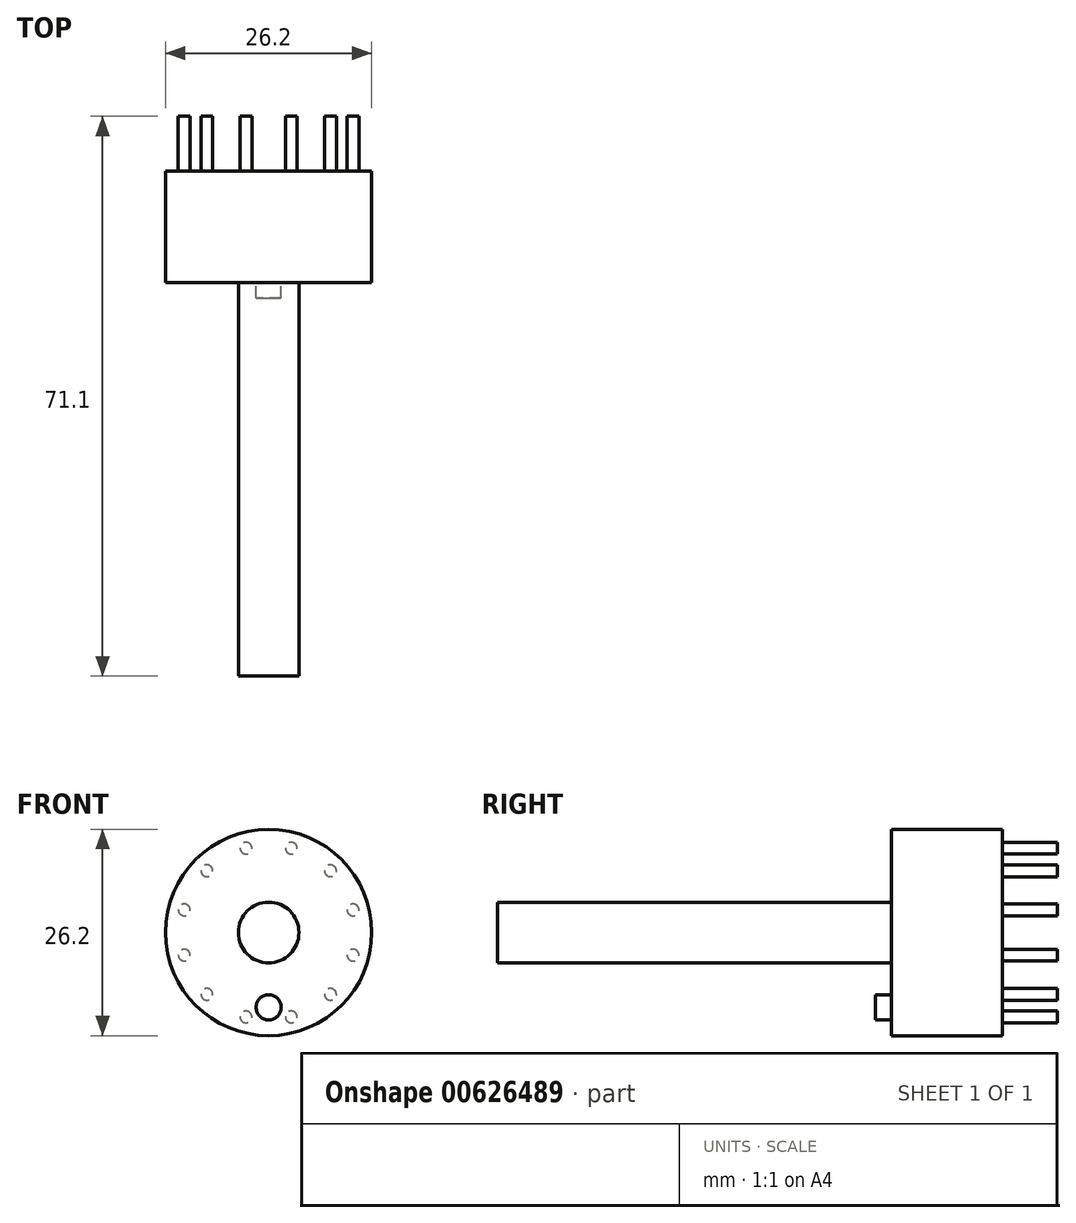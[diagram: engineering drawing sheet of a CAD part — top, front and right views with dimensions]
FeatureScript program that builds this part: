
annotation { "Feature Type Name" : "Feature", "Feature Type Description" : "" }
export const myFeature = defineFeature(function(context is Context, id is Id, definition is map)
    precondition{}
    {
        {
            var Q0;
            Q0=qCreatedBy(makeId("Front.planeOp"),FACE);
            var sketch = newSketch(context, id + "F0", { "sketchPlane" : qUnion([Q0])});
            skCircle(sketch, "E0", {"center": v(0, 0) * mm, "radius": 11.1 * mm, "construction": true});
            skCircle(sketch, "E1", {"center": v(0, 0) * mm, "radius": 3.85 * mm});
            skCircle(sketch, "E2", {"center": v(2.87, 10.72) * mm, "radius": 0.75 * mm});
            skLineSegment(sketch, "E3", {"start": v(2.87, 10.72) * mm, "end": v(3.6, 10.53) * mm, "construction": true});
            skLineSegment(sketch, "E4", {"start": v(2.87, 10.72) * mm, "end": v(3.07, 11.45) * mm, "construction": true});
            skCircle(sketch, "E5.1.0", {"center": v(-2.87, 10.72) * mm, "radius": 0.75 * mm});
            skCircle(sketch, "E5.2.0", {"center": v(-7.85, 7.85) * mm, "radius": 0.75 * mm});
            skCircle(sketch, "E5.3.0", {"center": v(-10.72, 2.87) * mm, "radius": 0.75 * mm});
            skCircle(sketch, "E5.4.0", {"center": v(-10.72, -2.87) * mm, "radius": 0.75 * mm});
            skCircle(sketch, "E5.5.0", {"center": v(-7.85, -7.85) * mm, "radius": 0.75 * mm});
            skCircle(sketch, "E5.6.0", {"center": v(-2.87, -10.72) * mm, "radius": 0.75 * mm});
            skCircle(sketch, "E5.7.0", {"center": v(2.87, -10.72) * mm, "radius": 0.75 * mm});
            skCircle(sketch, "E5.8.0", {"center": v(7.85, -7.85) * mm, "radius": 0.75 * mm});
            skCircle(sketch, "E5.9.0", {"center": v(10.72, -2.87) * mm, "radius": 0.75 * mm});
            skCircle(sketch, "E5.10.0", {"center": v(10.72, 2.87) * mm, "radius": 0.75 * mm});
            skCircle(sketch, "E5.11.0", {"center": v(7.85, 7.85) * mm, "radius": 0.75 * mm});
            skCircle(sketch, "E6", {"center": v(0, -9.5) * mm, "radius": 1.6 * mm});
            skCircle(sketch, "E7", {"center": v(0, 0) * mm, "radius": 13.1 * mm});
            skCircle(sketch, "E8", {"center": v(0, 0) * mm, "radius": 11.1 * mm});
            skSolve(sketch);
        }
        {
            var Q0;
            Q0 = qSketchRegion(id + "F0", true);
            var Q1;
            {var subQ0=sQuery(id+"F0.wireOp",EDGE,"E8");var subQ1=sQuery(id+"F0.wireOp",EDGE,"E2");var subQ2=makeQuery(id+"F0.imprint","INTERSECT",VERTEX,{"disambiguationData":[OD(0.0)],"derivedFrom":[subQ1,subQ0]});Q1=makeQuery(id+"F0.imprint","IMPRINT",FACE,{"disambiguationData":[TD([[makeQuery(id+"F0.imprint","IMPRINT",EDGE,{"disambiguationData":[TD([[subQ2,-1.0]])],"derivedFrom":subQ1}),1.0]])]});}
            var Q2;
            {var subQ0=sQuery(id+"F0.wireOp",EDGE,"E8");var subQ1=sQuery(id+"F0.wireOp",EDGE,"E5.1.0");var subQ2=makeQuery(id+"F0.imprint","INTERSECT",VERTEX,{"disambiguationData":[OD(0.0)],"derivedFrom":[subQ1,subQ0]});Q2=makeQuery(id+"F0.imprint","IMPRINT",FACE,{"disambiguationData":[TD([[makeQuery(id+"F0.imprint","IMPRINT",EDGE,{"disambiguationData":[TD([[subQ2,-1.0]])],"derivedFrom":subQ1}),1.0]])]});}
            var Q3;
            {var subQ0=sQuery(id+"F0.wireOp",EDGE,"E8");var subQ1=sQuery(id+"F0.wireOp",EDGE,"E5.11.0");var subQ2=makeQuery(id+"F0.imprint","INTERSECT",VERTEX,{"disambiguationData":[OD(0.0)],"derivedFrom":[subQ1,subQ0]});Q3=makeQuery(id+"F0.imprint","IMPRINT",FACE,{"disambiguationData":[TD([[makeQuery(id+"F0.imprint","IMPRINT",EDGE,{"disambiguationData":[TD([[subQ2,-1.0]])],"derivedFrom":subQ1}),1.0]])]});}
            var Q4;
            {var subQ0=sQuery(id+"F0.wireOp",EDGE,"E8");var subQ1=sQuery(id+"F0.wireOp",EDGE,"E5.10.0");var subQ2=makeQuery(id+"F0.imprint","INTERSECT",VERTEX,{"disambiguationData":[OD(0.0)],"derivedFrom":[subQ1,subQ0]});Q4=makeQuery(id+"F0.imprint","IMPRINT",FACE,{"disambiguationData":[TD([[makeQuery(id+"F0.imprint","IMPRINT",EDGE,{"disambiguationData":[TD([[subQ2,1.0]])],"derivedFrom":subQ1}),1.0]])]});}
            var Q5;
            {var subQ0=sQuery(id+"F0.wireOp",EDGE,"E8");var subQ1=sQuery(id+"F0.wireOp",EDGE,"E5.9.0");var subQ2=makeQuery(id+"F0.imprint","INTERSECT",VERTEX,{"disambiguationData":[OD(0.0)],"derivedFrom":[subQ1,subQ0]});Q5=makeQuery(id+"F0.imprint","IMPRINT",FACE,{"disambiguationData":[TD([[makeQuery(id+"F0.imprint","IMPRINT",EDGE,{"disambiguationData":[TD([[subQ2,-1.0]])],"derivedFrom":subQ1}),1.0]])]});}
            var Q6;
            {var subQ0=sQuery(id+"F0.wireOp",EDGE,"E8");var subQ1=sQuery(id+"F0.wireOp",EDGE,"E5.8.0");var subQ2=makeQuery(id+"F0.imprint","INTERSECT",VERTEX,{"disambiguationData":[OD(0.0)],"derivedFrom":[subQ1,subQ0]});Q6=makeQuery(id+"F0.imprint","IMPRINT",FACE,{"disambiguationData":[TD([[makeQuery(id+"F0.imprint","IMPRINT",EDGE,{"disambiguationData":[TD([[subQ2,-1.0]])],"derivedFrom":subQ1}),1.0]])]});}
            var Q7;
            {var subQ0=sQuery(id+"F0.wireOp",EDGE,"E8");var subQ1=sQuery(id+"F0.wireOp",EDGE,"E5.7.0");var subQ2=makeQuery(id+"F0.imprint","INTERSECT",VERTEX,{"disambiguationData":[OD(0.0)],"derivedFrom":[subQ1,subQ0]});Q7=makeQuery(id+"F0.imprint","IMPRINT",FACE,{"disambiguationData":[TD([[makeQuery(id+"F0.imprint","IMPRINT",EDGE,{"disambiguationData":[TD([[subQ2,-1.0]])],"derivedFrom":subQ1}),1.0]])]});}
            var Q8;
            {var subQ0=sQuery(id+"F0.wireOp",EDGE,"E8");var subQ1=sQuery(id+"F0.wireOp",EDGE,"E5.2.0");var subQ2=makeQuery(id+"F0.imprint","INTERSECT",VERTEX,{"disambiguationData":[OD(0.0)],"derivedFrom":[subQ1,subQ0]});Q8=makeQuery(id+"F0.imprint","IMPRINT",FACE,{"disambiguationData":[TD([[makeQuery(id+"F0.imprint","IMPRINT",EDGE,{"disambiguationData":[TD([[subQ2,-1.0]])],"derivedFrom":subQ1}),1.0]])]});}
            var Q9;
            {var subQ0=sQuery(id+"F0.wireOp",EDGE,"E8");var subQ1=sQuery(id+"F0.wireOp",EDGE,"E5.3.0");var subQ2=makeQuery(id+"F0.imprint","INTERSECT",VERTEX,{"disambiguationData":[OD(0.0)],"derivedFrom":[subQ1,subQ0]});Q9=makeQuery(id+"F0.imprint","IMPRINT",FACE,{"disambiguationData":[TD([[makeQuery(id+"F0.imprint","IMPRINT",EDGE,{"disambiguationData":[TD([[subQ2,-1.0]])],"derivedFrom":subQ1}),1.0]])]});}
            var Q10;
            {var subQ0=sQuery(id+"F0.wireOp",EDGE,"E8");var subQ1=sQuery(id+"F0.wireOp",EDGE,"E5.4.0");var subQ2=makeQuery(id+"F0.imprint","INTERSECT",VERTEX,{"disambiguationData":[OD(0.0)],"derivedFrom":[subQ1,subQ0]});Q10=makeQuery(id+"F0.imprint","IMPRINT",FACE,{"disambiguationData":[TD([[makeQuery(id+"F0.imprint","IMPRINT",EDGE,{"disambiguationData":[TD([[subQ2,-1.0]])],"derivedFrom":subQ1}),1.0]])]});}
            var Q11;
            {var subQ0=sQuery(id+"F0.wireOp",EDGE,"E8");var subQ1=sQuery(id+"F0.wireOp",EDGE,"E5.5.0");var subQ2=makeQuery(id+"F0.imprint","INTERSECT",VERTEX,{"disambiguationData":[OD(0.0)],"derivedFrom":[subQ1,subQ0]});Q11=makeQuery(id+"F0.imprint","IMPRINT",FACE,{"disambiguationData":[TD([[makeQuery(id+"F0.imprint","IMPRINT",EDGE,{"disambiguationData":[TD([[subQ2,-1.0]])],"derivedFrom":subQ1}),1.0]])]});}
            var Q12;
            {var subQ0=sQuery(id+"F0.wireOp",EDGE,"E8");var subQ1=sQuery(id+"F0.wireOp",EDGE,"E5.6.0");var subQ2=makeQuery(id+"F0.imprint","INTERSECT",VERTEX,{"disambiguationData":[OD(0.0)],"derivedFrom":[subQ1,subQ0]});Q12=makeQuery(id+"F0.imprint","IMPRINT",FACE,{"disambiguationData":[TD([[makeQuery(id+"F0.imprint","IMPRINT",EDGE,{"disambiguationData":[TD([[subQ2,-1.0]])],"derivedFrom":subQ1}),1.0]])]});}
            var Q13;
            Q13=makeQuery(id+"F0.imprint","IMPRINT",FACE,{"disambiguationData":[TD([[makeQuery(id+"F0.imprint","IMPRINT",EDGE,{"derivedFrom":sQuery(id+"F0.wireOp",EDGE,"E1")}),-1.0]])]});
            var Q14;
            {var subQ0=sQuery(id+"F0.wireOp",EDGE,"E8");var subQ1=sQuery(id+"F0.wireOp",EDGE,"E5.2.0");var subQ2=makeQuery(id+"F0.imprint","INTERSECT",VERTEX,{"disambiguationData":[OD(0.0)],"derivedFrom":[subQ1,subQ0]});Q14=makeQuery(id+"F0.imprint","IMPRINT",FACE,{"disambiguationData":[TD([[makeQuery(id+"F0.imprint","IMPRINT",EDGE,{"disambiguationData":[TD([[subQ2,1.0]])],"derivedFrom":subQ1}),1.0]])]});}
            var Q15;
            {var subQ0=sQuery(id+"F0.wireOp",EDGE,"E8");var subQ1=sQuery(id+"F0.wireOp",EDGE,"E5.1.0");var subQ2=makeQuery(id+"F0.imprint","INTERSECT",VERTEX,{"disambiguationData":[OD(0.0)],"derivedFrom":[subQ1,subQ0]});Q15=makeQuery(id+"F0.imprint","IMPRINT",FACE,{"disambiguationData":[TD([[makeQuery(id+"F0.imprint","IMPRINT",EDGE,{"disambiguationData":[TD([[subQ2,1.0]])],"derivedFrom":subQ1}),1.0]])]});}
            var Q16;
            {var subQ0=sQuery(id+"F0.wireOp",EDGE,"E8");var subQ1=sQuery(id+"F0.wireOp",EDGE,"E2");var subQ2=makeQuery(id+"F0.imprint","INTERSECT",VERTEX,{"disambiguationData":[OD(0.0)],"derivedFrom":[subQ1,subQ0]});Q16=makeQuery(id+"F0.imprint","IMPRINT",FACE,{"disambiguationData":[TD([[makeQuery(id+"F0.imprint","IMPRINT",EDGE,{"disambiguationData":[TD([[subQ2,1.0]])],"derivedFrom":subQ1}),1.0]])]});}
            var Q17;
            {var subQ0=sQuery(id+"F0.wireOp",EDGE,"E8");var subQ1=sQuery(id+"F0.wireOp",EDGE,"E5.11.0");var subQ2=makeQuery(id+"F0.imprint","INTERSECT",VERTEX,{"disambiguationData":[OD(0.0)],"derivedFrom":[subQ1,subQ0]});Q17=makeQuery(id+"F0.imprint","IMPRINT",FACE,{"disambiguationData":[TD([[makeQuery(id+"F0.imprint","IMPRINT",EDGE,{"disambiguationData":[TD([[subQ2,1.0]])],"derivedFrom":subQ1}),1.0]])]});}
            var Q18;
            {var subQ0=sQuery(id+"F0.wireOp",EDGE,"E8");var subQ1=sQuery(id+"F0.wireOp",EDGE,"E5.10.0");var subQ2=makeQuery(id+"F0.imprint","INTERSECT",VERTEX,{"disambiguationData":[OD(0.0)],"derivedFrom":[subQ1,subQ0]});Q18=makeQuery(id+"F0.imprint","IMPRINT",FACE,{"disambiguationData":[TD([[makeQuery(id+"F0.imprint","IMPRINT",EDGE,{"disambiguationData":[TD([[subQ2,-1.0]])],"derivedFrom":subQ1}),1.0]])]});}
            var Q19;
            {var subQ0=sQuery(id+"F0.wireOp",EDGE,"E8");var subQ1=sQuery(id+"F0.wireOp",EDGE,"E5.9.0");var subQ2=makeQuery(id+"F0.imprint","INTERSECT",VERTEX,{"disambiguationData":[OD(0.0)],"derivedFrom":[subQ1,subQ0]});Q19=makeQuery(id+"F0.imprint","IMPRINT",FACE,{"disambiguationData":[TD([[makeQuery(id+"F0.imprint","IMPRINT",EDGE,{"disambiguationData":[TD([[subQ2,1.0]])],"derivedFrom":subQ1}),1.0]])]});}
            var Q20;
            {var subQ0=sQuery(id+"F0.wireOp",EDGE,"E8");var subQ1=sQuery(id+"F0.wireOp",EDGE,"E5.8.0");var subQ2=makeQuery(id+"F0.imprint","INTERSECT",VERTEX,{"disambiguationData":[OD(0.0)],"derivedFrom":[subQ1,subQ0]});Q20=makeQuery(id+"F0.imprint","IMPRINT",FACE,{"disambiguationData":[TD([[makeQuery(id+"F0.imprint","IMPRINT",EDGE,{"disambiguationData":[TD([[subQ2,1.0]])],"derivedFrom":subQ1}),1.0]])]});}
            var Q21;
            {var subQ0=sQuery(id+"F0.wireOp",EDGE,"E8");var subQ1=sQuery(id+"F0.wireOp",EDGE,"E5.7.0");var subQ2=makeQuery(id+"F0.imprint","INTERSECT",VERTEX,{"disambiguationData":[OD(0.0)],"derivedFrom":[subQ1,subQ0]});Q21=makeQuery(id+"F0.imprint","IMPRINT",FACE,{"disambiguationData":[TD([[makeQuery(id+"F0.imprint","IMPRINT",EDGE,{"disambiguationData":[TD([[subQ2,1.0]])],"derivedFrom":subQ1}),1.0]])]});}
            var Q22;
            {var subQ0=sQuery(id+"F0.wireOp",EDGE,"E8");var subQ1=sQuery(id+"F0.wireOp",EDGE,"E5.6.0");var subQ2=makeQuery(id+"F0.imprint","INTERSECT",VERTEX,{"disambiguationData":[OD(0.0)],"derivedFrom":[subQ1,subQ0]});Q22=makeQuery(id+"F0.imprint","IMPRINT",FACE,{"disambiguationData":[TD([[makeQuery(id+"F0.imprint","IMPRINT",EDGE,{"disambiguationData":[TD([[subQ2,1.0]])],"derivedFrom":subQ1}),1.0]])]});}
            var Q23;
            {var subQ0=sQuery(id+"F0.wireOp",EDGE,"E8");var subQ1=sQuery(id+"F0.wireOp",EDGE,"E5.5.0");var subQ2=makeQuery(id+"F0.imprint","INTERSECT",VERTEX,{"disambiguationData":[OD(0.0)],"derivedFrom":[subQ1,subQ0]});Q23=makeQuery(id+"F0.imprint","IMPRINT",FACE,{"disambiguationData":[TD([[makeQuery(id+"F0.imprint","IMPRINT",EDGE,{"disambiguationData":[TD([[subQ2,1.0]])],"derivedFrom":subQ1}),1.0]])]});}
            var Q24;
            {var subQ0=sQuery(id+"F0.wireOp",EDGE,"E8");var subQ1=sQuery(id+"F0.wireOp",EDGE,"E5.4.0");var subQ2=makeQuery(id+"F0.imprint","INTERSECT",VERTEX,{"disambiguationData":[OD(0.0)],"derivedFrom":[subQ1,subQ0]});Q24=makeQuery(id+"F0.imprint","IMPRINT",FACE,{"disambiguationData":[TD([[makeQuery(id+"F0.imprint","IMPRINT",EDGE,{"disambiguationData":[TD([[subQ2,1.0]])],"derivedFrom":subQ1}),1.0]])]});}
            var Q25;
            {var subQ0=sQuery(id+"F0.wireOp",EDGE,"E8");var subQ1=sQuery(id+"F0.wireOp",EDGE,"E5.3.0");var subQ2=makeQuery(id+"F0.imprint","INTERSECT",VERTEX,{"disambiguationData":[OD(0.0)],"derivedFrom":[subQ1,subQ0]});Q25=makeQuery(id+"F0.imprint","IMPRINT",FACE,{"disambiguationData":[TD([[makeQuery(id+"F0.imprint","IMPRINT",EDGE,{"disambiguationData":[TD([[subQ2,1.0]])],"derivedFrom":subQ1}),1.0]])]});}
            extrude(context, id + "F1", {"entities" : qUnion([Q0, Q1, Q2, Q3, Q4, Q5, Q6, Q7, Q8, Q9, Q10, Q11, Q12, Q13, Q14, Q15, Q16, Q17, Q18, Q19, Q20, Q21, Q22, Q23, Q24, Q25]), "depth" : 14.1 * mm, "offsetDistance" : 25 * mm});
        }
        {
            var Q0;
            Q0=makeQuery(id+"F0.imprint","IMPRINT",FACE,{"disambiguationData":[TD([[makeQuery(id+"F0.imprint","IMPRINT",EDGE,{"derivedFrom":sQuery(id+"F0.wireOp",EDGE,"E6")}),1.0]])]});
            var Q1;
            Q1=makeQuery(id+"F1.opExtrude","CAP_FACE",FACE,{"disambiguationData":[OSD([sQuery(id+"F0.wireOp",EDGE,"E1"),sQuery(id+"F0.wireOp",EDGE,"E6"),sQuery(id+"F0.wireOp",EDGE,"E7")])],"isStart":false});
            extrude(context, id + "F2", {"entities" : qUnion([Q0]), "operationType" : NewBodyOperationType.ADD, "endBound" : BoundingType.UP_TO_SURFACE, "depth" : 25 * mm, "endBoundEntityFace" : qUnion([Q1]), "hasOffset" : true, "offsetDistance" : -2 * mm});
        }
        {
            var Q0;
            Q0=makeQuery(id+"F0.imprint","IMPRINT",FACE,{"disambiguationData":[TD([[makeQuery(id+"F0.imprint","IMPRINT",EDGE,{"derivedFrom":sQuery(id+"F0.wireOp",EDGE,"E1")}),1.0]])]});
            var Q1;
            Q1=makeQuery(id+"F1.opExtrude","CAP_FACE",FACE,{"disambiguationData":[OSD([sQuery(id+"F0.wireOp",EDGE,"E1"),sQuery(id+"F0.wireOp",EDGE,"E6"),sQuery(id+"F0.wireOp",EDGE,"E7")])],"isStart":false});
            extrude(context, id + "F3", {"entities" : qUnion([Q0]), "operationType" : NewBodyOperationType.ADD, "endBound" : BoundingType.UP_TO_SURFACE, "depth" : 34.9 * mm, "endBoundEntityFace" : qUnion([Q1]), "hasOffset" : true, "offsetDistance" : -50 * mm});
        }
        {
            var Q0;
            {var subQ0=sQuery(id+"F0.wireOp",EDGE,"E8");var subQ1=sQuery(id+"F0.wireOp",EDGE,"E5.7.0");var subQ2=makeQuery(id+"F0.imprint","INTERSECT",VERTEX,{"disambiguationData":[OD(0.0)],"derivedFrom":[subQ1,subQ0]});Q0=makeQuery(id+"F0.imprint","IMPRINT",FACE,{"disambiguationData":[TD([[makeQuery(id+"F0.imprint","IMPRINT",EDGE,{"disambiguationData":[TD([[subQ2,1.0]])],"derivedFrom":subQ1}),1.0]])]});}
            var Q1;
            {var subQ0=sQuery(id+"F0.wireOp",EDGE,"E8");var subQ1=sQuery(id+"F0.wireOp",EDGE,"E5.7.0");var subQ2=makeQuery(id+"F0.imprint","INTERSECT",VERTEX,{"disambiguationData":[OD(0.0)],"derivedFrom":[subQ1,subQ0]});Q1=makeQuery(id+"F0.imprint","IMPRINT",FACE,{"disambiguationData":[TD([[makeQuery(id+"F0.imprint","IMPRINT",EDGE,{"disambiguationData":[TD([[subQ2,-1.0]])],"derivedFrom":subQ1}),1.0]])]});}
            var Q2;
            {var subQ0=sQuery(id+"F0.wireOp",EDGE,"E8");var subQ1=sQuery(id+"F0.wireOp",EDGE,"E5.8.0");var subQ2=makeQuery(id+"F0.imprint","INTERSECT",VERTEX,{"disambiguationData":[OD(0.0)],"derivedFrom":[subQ1,subQ0]});Q2=makeQuery(id+"F0.imprint","IMPRINT",FACE,{"disambiguationData":[TD([[makeQuery(id+"F0.imprint","IMPRINT",EDGE,{"disambiguationData":[TD([[subQ2,1.0]])],"derivedFrom":subQ1}),1.0]])]});}
            var Q3;
            {var subQ0=sQuery(id+"F0.wireOp",EDGE,"E8");var subQ1=sQuery(id+"F0.wireOp",EDGE,"E5.8.0");var subQ2=makeQuery(id+"F0.imprint","INTERSECT",VERTEX,{"disambiguationData":[OD(0.0)],"derivedFrom":[subQ1,subQ0]});Q3=makeQuery(id+"F0.imprint","IMPRINT",FACE,{"disambiguationData":[TD([[makeQuery(id+"F0.imprint","IMPRINT",EDGE,{"disambiguationData":[TD([[subQ2,-1.0]])],"derivedFrom":subQ1}),1.0]])]});}
            var Q4;
            {var subQ0=sQuery(id+"F0.wireOp",EDGE,"E8");var subQ1=sQuery(id+"F0.wireOp",EDGE,"E5.9.0");var subQ2=makeQuery(id+"F0.imprint","INTERSECT",VERTEX,{"disambiguationData":[OD(0.0)],"derivedFrom":[subQ1,subQ0]});Q4=makeQuery(id+"F0.imprint","IMPRINT",FACE,{"disambiguationData":[TD([[makeQuery(id+"F0.imprint","IMPRINT",EDGE,{"disambiguationData":[TD([[subQ2,1.0]])],"derivedFrom":subQ1}),1.0]])]});}
            var Q5;
            {var subQ0=sQuery(id+"F0.wireOp",EDGE,"E8");var subQ1=sQuery(id+"F0.wireOp",EDGE,"E5.9.0");var subQ2=makeQuery(id+"F0.imprint","INTERSECT",VERTEX,{"disambiguationData":[OD(0.0)],"derivedFrom":[subQ1,subQ0]});Q5=makeQuery(id+"F0.imprint","IMPRINT",FACE,{"disambiguationData":[TD([[makeQuery(id+"F0.imprint","IMPRINT",EDGE,{"disambiguationData":[TD([[subQ2,-1.0]])],"derivedFrom":subQ1}),1.0]])]});}
            var Q6;
            {var subQ0=sQuery(id+"F0.wireOp",EDGE,"E8");var subQ1=sQuery(id+"F0.wireOp",EDGE,"E5.6.0");var subQ2=makeQuery(id+"F0.imprint","INTERSECT",VERTEX,{"disambiguationData":[OD(0.0)],"derivedFrom":[subQ1,subQ0]});Q6=makeQuery(id+"F0.imprint","IMPRINT",FACE,{"disambiguationData":[TD([[makeQuery(id+"F0.imprint","IMPRINT",EDGE,{"disambiguationData":[TD([[subQ2,-1.0]])],"derivedFrom":subQ1}),1.0]])]});}
            var Q7;
            {var subQ0=sQuery(id+"F0.wireOp",EDGE,"E8");var subQ1=sQuery(id+"F0.wireOp",EDGE,"E5.6.0");var subQ2=makeQuery(id+"F0.imprint","INTERSECT",VERTEX,{"disambiguationData":[OD(0.0)],"derivedFrom":[subQ1,subQ0]});Q7=makeQuery(id+"F0.imprint","IMPRINT",FACE,{"disambiguationData":[TD([[makeQuery(id+"F0.imprint","IMPRINT",EDGE,{"disambiguationData":[TD([[subQ2,1.0]])],"derivedFrom":subQ1}),1.0]])]});}
            var Q8;
            {var subQ0=sQuery(id+"F0.wireOp",EDGE,"E8");var subQ1=sQuery(id+"F0.wireOp",EDGE,"E5.5.0");var subQ2=makeQuery(id+"F0.imprint","INTERSECT",VERTEX,{"disambiguationData":[OD(0.0)],"derivedFrom":[subQ1,subQ0]});Q8=makeQuery(id+"F0.imprint","IMPRINT",FACE,{"disambiguationData":[TD([[makeQuery(id+"F0.imprint","IMPRINT",EDGE,{"disambiguationData":[TD([[subQ2,-1.0]])],"derivedFrom":subQ1}),1.0]])]});}
            var Q9;
            {var subQ0=sQuery(id+"F0.wireOp",EDGE,"E8");var subQ1=sQuery(id+"F0.wireOp",EDGE,"E5.5.0");var subQ2=makeQuery(id+"F0.imprint","INTERSECT",VERTEX,{"disambiguationData":[OD(0.0)],"derivedFrom":[subQ1,subQ0]});Q9=makeQuery(id+"F0.imprint","IMPRINT",FACE,{"disambiguationData":[TD([[makeQuery(id+"F0.imprint","IMPRINT",EDGE,{"disambiguationData":[TD([[subQ2,1.0]])],"derivedFrom":subQ1}),1.0]])]});}
            var Q10;
            {var subQ0=sQuery(id+"F0.wireOp",EDGE,"E8");var subQ1=sQuery(id+"F0.wireOp",EDGE,"E5.4.0");var subQ2=makeQuery(id+"F0.imprint","INTERSECT",VERTEX,{"disambiguationData":[OD(0.0)],"derivedFrom":[subQ1,subQ0]});Q10=makeQuery(id+"F0.imprint","IMPRINT",FACE,{"disambiguationData":[TD([[makeQuery(id+"F0.imprint","IMPRINT",EDGE,{"disambiguationData":[TD([[subQ2,1.0]])],"derivedFrom":subQ1}),1.0]])]});}
            var Q11;
            {var subQ0=sQuery(id+"F0.wireOp",EDGE,"E8");var subQ1=sQuery(id+"F0.wireOp",EDGE,"E5.4.0");var subQ2=makeQuery(id+"F0.imprint","INTERSECT",VERTEX,{"disambiguationData":[OD(0.0)],"derivedFrom":[subQ1,subQ0]});Q11=makeQuery(id+"F0.imprint","IMPRINT",FACE,{"disambiguationData":[TD([[makeQuery(id+"F0.imprint","IMPRINT",EDGE,{"disambiguationData":[TD([[subQ2,-1.0]])],"derivedFrom":subQ1}),1.0]])]});}
            var Q12;
            {var subQ0=sQuery(id+"F0.wireOp",EDGE,"E8");var subQ1=sQuery(id+"F0.wireOp",EDGE,"E5.3.0");var subQ2=makeQuery(id+"F0.imprint","INTERSECT",VERTEX,{"disambiguationData":[OD(0.0)],"derivedFrom":[subQ1,subQ0]});Q12=makeQuery(id+"F0.imprint","IMPRINT",FACE,{"disambiguationData":[TD([[makeQuery(id+"F0.imprint","IMPRINT",EDGE,{"disambiguationData":[TD([[subQ2,1.0]])],"derivedFrom":subQ1}),1.0]])]});}
            var Q13;
            {var subQ0=sQuery(id+"F0.wireOp",EDGE,"E8");var subQ1=sQuery(id+"F0.wireOp",EDGE,"E5.3.0");var subQ2=makeQuery(id+"F0.imprint","INTERSECT",VERTEX,{"disambiguationData":[OD(0.0)],"derivedFrom":[subQ1,subQ0]});Q13=makeQuery(id+"F0.imprint","IMPRINT",FACE,{"disambiguationData":[TD([[makeQuery(id+"F0.imprint","IMPRINT",EDGE,{"disambiguationData":[TD([[subQ2,-1.0]])],"derivedFrom":subQ1}),1.0]])]});}
            var Q14;
            {var subQ0=sQuery(id+"F0.wireOp",EDGE,"E8");var subQ1=sQuery(id+"F0.wireOp",EDGE,"E5.2.0");var subQ2=makeQuery(id+"F0.imprint","INTERSECT",VERTEX,{"disambiguationData":[OD(0.0)],"derivedFrom":[subQ1,subQ0]});Q14=makeQuery(id+"F0.imprint","IMPRINT",FACE,{"disambiguationData":[TD([[makeQuery(id+"F0.imprint","IMPRINT",EDGE,{"disambiguationData":[TD([[subQ2,1.0]])],"derivedFrom":subQ1}),1.0]])]});}
            var Q15;
            {var subQ0=sQuery(id+"F0.wireOp",EDGE,"E8");var subQ1=sQuery(id+"F0.wireOp",EDGE,"E5.2.0");var subQ2=makeQuery(id+"F0.imprint","INTERSECT",VERTEX,{"disambiguationData":[OD(0.0)],"derivedFrom":[subQ1,subQ0]});Q15=makeQuery(id+"F0.imprint","IMPRINT",FACE,{"disambiguationData":[TD([[makeQuery(id+"F0.imprint","IMPRINT",EDGE,{"disambiguationData":[TD([[subQ2,-1.0]])],"derivedFrom":subQ1}),1.0]])]});}
            var Q16;
            {var subQ0=sQuery(id+"F0.wireOp",EDGE,"E8");var subQ1=sQuery(id+"F0.wireOp",EDGE,"E2");var subQ2=makeQuery(id+"F0.imprint","INTERSECT",VERTEX,{"disambiguationData":[OD(0.0)],"derivedFrom":[subQ1,subQ0]});Q16=makeQuery(id+"F0.imprint","IMPRINT",FACE,{"disambiguationData":[TD([[makeQuery(id+"F0.imprint","IMPRINT",EDGE,{"disambiguationData":[TD([[subQ2,1.0]])],"derivedFrom":subQ1}),1.0]])]});}
            var Q17;
            {var subQ0=sQuery(id+"F0.wireOp",EDGE,"E8");var subQ1=sQuery(id+"F0.wireOp",EDGE,"E2");var subQ2=makeQuery(id+"F0.imprint","INTERSECT",VERTEX,{"disambiguationData":[OD(0.0)],"derivedFrom":[subQ1,subQ0]});Q17=makeQuery(id+"F0.imprint","IMPRINT",FACE,{"disambiguationData":[TD([[makeQuery(id+"F0.imprint","IMPRINT",EDGE,{"disambiguationData":[TD([[subQ2,-1.0]])],"derivedFrom":subQ1}),1.0]])]});}
            var Q18;
            {var subQ0=sQuery(id+"F0.wireOp",EDGE,"E8");var subQ1=sQuery(id+"F0.wireOp",EDGE,"E5.10.0");var subQ2=makeQuery(id+"F0.imprint","INTERSECT",VERTEX,{"disambiguationData":[OD(0.0)],"derivedFrom":[subQ1,subQ0]});Q18=makeQuery(id+"F0.imprint","IMPRINT",FACE,{"disambiguationData":[TD([[makeQuery(id+"F0.imprint","IMPRINT",EDGE,{"disambiguationData":[TD([[subQ2,-1.0]])],"derivedFrom":subQ1}),1.0]])]});}
            var Q19;
            {var subQ0=sQuery(id+"F0.wireOp",EDGE,"E8");var subQ1=sQuery(id+"F0.wireOp",EDGE,"E5.10.0");var subQ2=makeQuery(id+"F0.imprint","INTERSECT",VERTEX,{"disambiguationData":[OD(0.0)],"derivedFrom":[subQ1,subQ0]});Q19=makeQuery(id+"F0.imprint","IMPRINT",FACE,{"disambiguationData":[TD([[makeQuery(id+"F0.imprint","IMPRINT",EDGE,{"disambiguationData":[TD([[subQ2,1.0]])],"derivedFrom":subQ1}),1.0]])]});}
            var Q20;
            {var subQ0=sQuery(id+"F0.wireOp",EDGE,"E8");var subQ1=sQuery(id+"F0.wireOp",EDGE,"E5.11.0");var subQ2=makeQuery(id+"F0.imprint","INTERSECT",VERTEX,{"disambiguationData":[OD(0.0)],"derivedFrom":[subQ1,subQ0]});Q20=makeQuery(id+"F0.imprint","IMPRINT",FACE,{"disambiguationData":[TD([[makeQuery(id+"F0.imprint","IMPRINT",EDGE,{"disambiguationData":[TD([[subQ2,1.0]])],"derivedFrom":subQ1}),1.0]])]});}
            var Q21;
            {var subQ0=sQuery(id+"F0.wireOp",EDGE,"E8");var subQ1=sQuery(id+"F0.wireOp",EDGE,"E5.11.0");var subQ2=makeQuery(id+"F0.imprint","INTERSECT",VERTEX,{"disambiguationData":[OD(0.0)],"derivedFrom":[subQ1,subQ0]});Q21=makeQuery(id+"F0.imprint","IMPRINT",FACE,{"disambiguationData":[TD([[makeQuery(id+"F0.imprint","IMPRINT",EDGE,{"disambiguationData":[TD([[subQ2,-1.0]])],"derivedFrom":subQ1}),1.0]])]});}
            var Q22;
            {var subQ0=sQuery(id+"F0.wireOp",EDGE,"E8");var subQ1=sQuery(id+"F0.wireOp",EDGE,"E5.1.0");var subQ2=makeQuery(id+"F0.imprint","INTERSECT",VERTEX,{"disambiguationData":[OD(0.0)],"derivedFrom":[subQ1,subQ0]});Q22=makeQuery(id+"F0.imprint","IMPRINT",FACE,{"disambiguationData":[TD([[makeQuery(id+"F0.imprint","IMPRINT",EDGE,{"disambiguationData":[TD([[subQ2,1.0]])],"derivedFrom":subQ1}),1.0]])]});}
            var Q23;
            {var subQ0=sQuery(id+"F0.wireOp",EDGE,"E8");var subQ1=sQuery(id+"F0.wireOp",EDGE,"E5.1.0");var subQ2=makeQuery(id+"F0.imprint","INTERSECT",VERTEX,{"disambiguationData":[OD(0.0)],"derivedFrom":[subQ1,subQ0]});Q23=makeQuery(id+"F0.imprint","IMPRINT",FACE,{"disambiguationData":[TD([[makeQuery(id+"F0.imprint","IMPRINT",EDGE,{"disambiguationData":[TD([[subQ2,-1.0]])],"derivedFrom":subQ1}),1.0]])]});}
            extrude(context, id + "F4", {"entities" : qUnion([Q0, Q1, Q2, Q3, Q4, Q5, Q6, Q7, Q8, Q9, Q10, Q11, Q12, Q13, Q14, Q15, Q16, Q17, Q18, Q19, Q20, Q21, Q22, Q23]), "operationType" : NewBodyOperationType.ADD, "oppositeDirection" : true, "depth" : 7 * mm, "offsetDistance" : 25 * mm});
        }
    });
